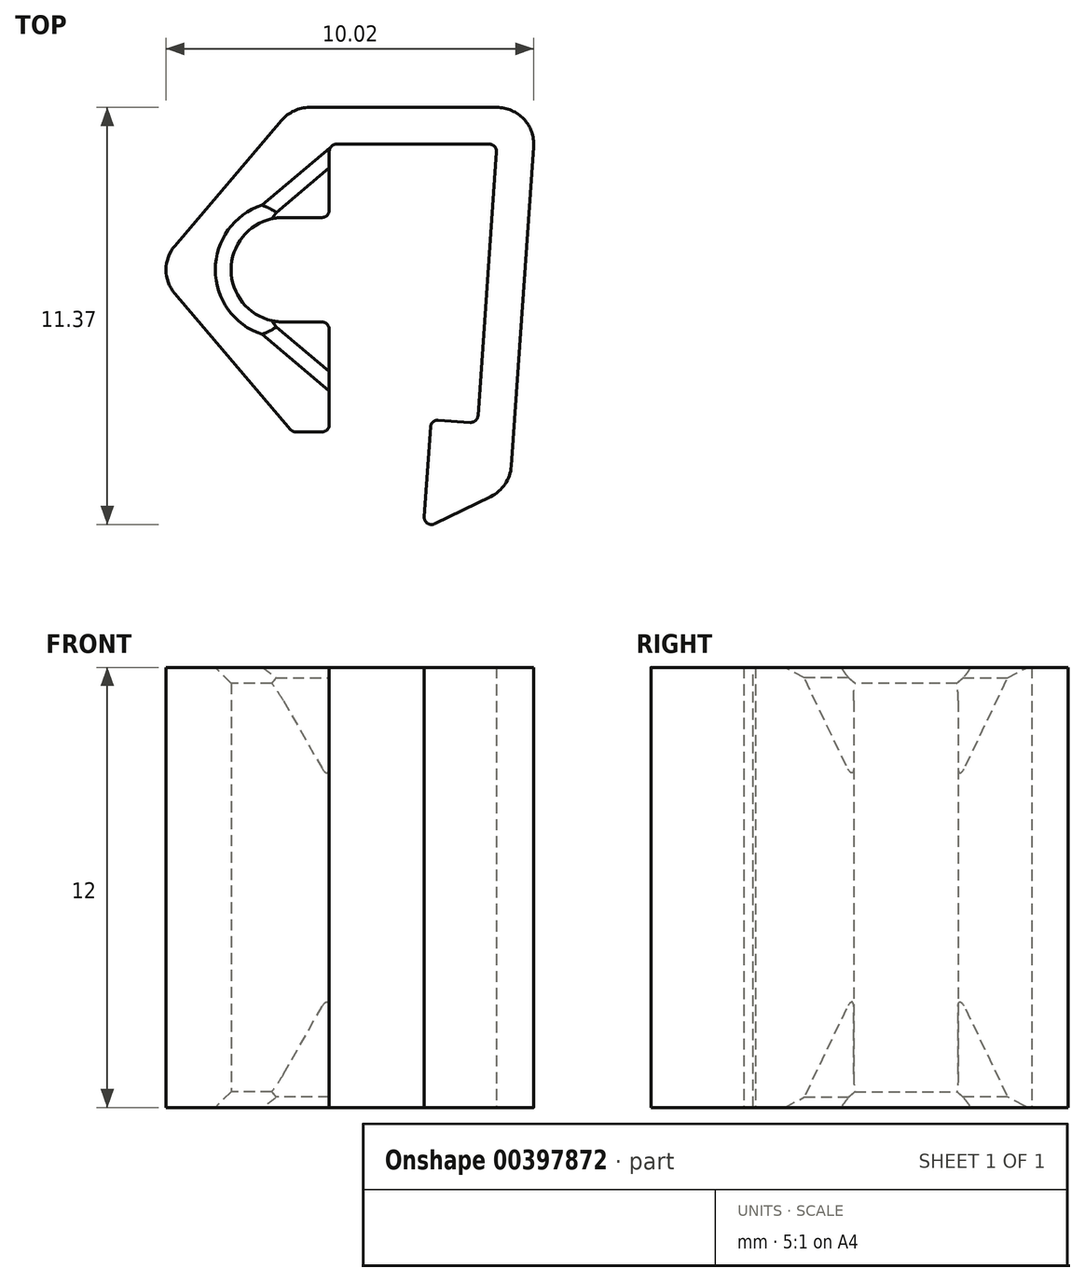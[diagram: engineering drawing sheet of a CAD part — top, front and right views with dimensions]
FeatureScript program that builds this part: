
annotation { "Feature Type Name" : "Feature", "Feature Type Description" : "" }
export const myFeature = defineFeature(function(context is Context, id is Id, definition is map)
    precondition{}
    {
        {
            var Q0;
            Q0=qCreatedBy(makeId("Top.planeOp"),FACE);
            var sketch = newSketch(context, id + "F0", { "sketchPlane" : qUnion([Q0])});
            skLineSegment(sketch, "E0", {"start": v(0, 0) * mm, "end": v(-0.53, -7.6) * mm});
            skLineSegment(sketch, "E1", {"start": v(-0.53, -7.6) * mm, "end": v(-1.8, -7.51) * mm});
            skLineSegment(sketch, "E2", {"start": v(-1.8, -7.51) * mm, "end": v(-2, -10.5) * mm});
            skLineSegment(sketch, "E3", {"start": v(-2, -10.5) * mm, "end": v(0.35, -9.36) * mm});
            skLineSegment(sketch, "E4", {"start": v(0.35, -9.36) * mm, "end": v(1.07, 1) * mm});
            skLineSegment(sketch, "E5", {"start": v(1.07, 1) * mm, "end": v(-5.57, 1) * mm});
            skLineSegment(sketch, "E6", {"start": v(-5.82, -4.85) * mm, "end": v(-4.57, -4.85) * mm});
            skLineSegment(sketch, "E7", {"start": v(-4.57, -4.85) * mm, "end": v(-4.57, -7.85) * mm});
            skLineSegment(sketch, "E8", {"start": v(-9.33, -3.43) * mm, "end": v(-5.57, -7.85) * mm});
            skLineSegment(sketch, "E9", {"start": v(-5.57, -7.85) * mm, "end": v(-4.57, -7.85) * mm});
            skLineSegment(sketch, "E10", {"start": v(-4.57, -2) * mm, "end": v(-5.82, -2) * mm});
            skLineSegment(sketch, "E11", {"start": v(0, 0) * mm, "end": v(-4.57, 0) * mm});
            skLineSegment(sketch, "E12", {"start": v(-4.57, 0) * mm, "end": v(-4.57, -2) * mm});
            skArc(sketch, "E13", {"start": v(-5.82, -2) * mm, "mid": v(-7.25, -3.43) * mm, "end": v(-5.82, -4.85) * mm});
            skLineSegment(sketch, "E14", {"start": v(-9.33, -3.43) * mm, "end": v(-5.57, 1) * mm});
            skLineSegment(sketch, "E15", {"start": v(-5.57, -7.85) * mm, "end": v(-5.57, 1) * mm, "construction": true});
            skLineSegment(sketch, "E16", {"start": v(-5.82, -3.43) * mm, "end": v(-6.9, -2.5) * mm, "construction": true});
            skLineSegment(sketch, "E17", {"start": v(-6.9, -2.5) * mm, "end": v(-7.86, -1.7) * mm, "construction": true});
            skLineSegment(sketch, "E18", {"start": v(0, 0) * mm, "end": v(0, 1) * mm, "construction": true});
            skLineSegment(sketch, "E19", {"start": v(1, -0.07) * mm, "end": v(0, 0) * mm, "construction": true});
            skLineSegment(sketch, "E20", {"start": v(-6.9, -4.35) * mm, "end": v(-7.86, -5.16) * mm, "construction": true});
            skSolve(sketch);
        }
        {
            var Q0;
            Q0=qSketchRegion(id+"F0",true);
            extrude(context, id + "F1", {"entities" : qUnion([Q0]), "depth" : 6 * mm});
        }
        {
            var Q0;
            Q0=makeQuery(id+"F1.opExtrude","CAP_FACE",FACE,{"disambiguationData":[OSD([sQuery(id+"F0.wireOp",EDGE,"E0"),sQuery(id+"F0.wireOp",EDGE,"E1"),sQuery(id+"F0.wireOp",EDGE,"E2"),sQuery(id+"F0.wireOp",EDGE,"E3"),sQuery(id+"F0.wireOp",EDGE,"E4"),sQuery(id+"F0.wireOp",EDGE,"E5"),sQuery(id+"F0.wireOp",EDGE,"3qQk4eZ2-qFBK-7vCE-47k8-9gwiF50xY8QG"),sQuery(id+"F0.wireOp",EDGE,"FwfflrWr-MbD4-lGZ7-AJjG-6BkzjliF19me"),sQuery(id+"F0.wireOp",EDGE,"E6"),sQuery(id+"F0.wireOp",EDGE,"E7"),sQuery(id+"F0.wireOp",EDGE,"dEJFUDGW-VdPt-nXIw-TINV-OlQtnsbTHH9Y"),sQuery(id+"F0.wireOp",EDGE,"E8"),sQuery(id+"F0.wireOp",EDGE,"E9")])],"isStart":false});
            var sketch = newSketch(context, id + "F2", { "sketchPlane" : qUnion([Q0])});
            skLineSegment(sketch, "E21", {"start": v(-6.74, -4.52) * mm, "end": v(-4.57, -6.33) * mm});
            skLineSegment(sketch, "E22", {"start": v(-4.57, -6.33) * mm, "end": v(-4.57, -4.85) * mm});
            skLineSegment(sketch, "E23", {"start": v(-4.57, -4.85) * mm, "end": v(-6.74, -4.52) * mm});
            skLineSegment(sketch, "E24", {"start": v(-6.74, -2.33) * mm, "end": v(-4.57, -0.52) * mm});
            skLineSegment(sketch, "E25", {"start": v(-4.57, -0.52) * mm, "end": v(-4.57, -2) * mm});
            skLineSegment(sketch, "E26", {"start": v(-4.57, -2) * mm, "end": v(-6.74, -2.33) * mm});
            skSolve(sketch);
        }
        {
            var Q0;
            Q0=qSketchRegion(id+"F2",true);
            extrude(context, id + "F3", {"entities" : qUnion([Q0]), "operationType" : NewBodyOperationType.REMOVE, "oppositeDirection" : true, "depth" : 3 * mm});
        }
        {
            var Q0;
            Q0=makeQuery(id+"F3.boolean.opBoolean","COPY",EDGE,{"derivedFrom":makeQuery(id+"F3.opExtrude","CAP_EDGE",EDGE,{"disambiguationData":[OSD([sQuery(id+"F2.wireOp",EDGE,"E21")])],"isStart":false})});
            chamfer(context, id + "F4", {"entities" : qUnion([Q0]), "chamferType" : ChamferType.TWO_OFFSETS, "width1" : 1.1 * mm, "oppositeDirection" : false, "width2" : 3 * mm, "tangentPropagation" : true});
        }
        {
            var Q0;
            Q0=makeQuery(id+"F3.boolean.opBoolean","COPY",EDGE,{"derivedFrom":makeQuery(id+"F3.opExtrude","CAP_EDGE",EDGE,{"disambiguationData":[OSD([sQuery(id+"F2.wireOp",EDGE,"E24")])],"isStart":false})});
            chamfer(context, id + "F5", {"entities" : qUnion([Q0]), "chamferType" : ChamferType.TWO_OFFSETS, "width1" : 3 * mm, "oppositeDirection" : false, "width2" : 1.1 * mm, "tangentPropagation" : true});
        }
        {
            var Q0;
            Q0=makeQuery(id+"F1.opExtrude","SWEPT_EDGE",EDGE,{"disambiguationData":[OSD([sQuery(id+"F0.wireOp",EDGE,"E0"),sQuery(id+"F0.wireOp",EDGE,"3qQk4eZ2-qFBK-7vCE-47k8-9gwiF50xY8QG")])]});
            var Q1;
            Q1=makeQuery(id+"F1.opExtrude","SWEPT_EDGE",EDGE,{"disambiguationData":[OSD([sQuery(id+"F0.wireOp",EDGE,"E0"),sQuery(id+"F0.wireOp",EDGE,"E1")])]});
            var Q2;
            Q2=makeQuery(id+"F1.opExtrude","SWEPT_EDGE",EDGE,{"disambiguationData":[OSD([sQuery(id+"F0.wireOp",EDGE,"E1"),sQuery(id+"F0.wireOp",EDGE,"E2")])]});
            var Q3;
            Q3=makeQuery(id+"F1.opExtrude","SWEPT_EDGE",EDGE,{"disambiguationData":[OSD([sQuery(id+"F0.wireOp",EDGE,"E2"),sQuery(id+"F0.wireOp",EDGE,"E3")])]});
            var Q4;
            Q4=makeQuery(id+"F1.opExtrude","SWEPT_EDGE",EDGE,{"disambiguationData":[OSD([sQuery(id+"F0.wireOp",EDGE,"E7"),sQuery(id+"F0.wireOp",EDGE,"E9")])]});
            var Q5;
            Q5=makeQuery(id+"F1.opExtrude","SWEPT_EDGE",EDGE,{"disambiguationData":[OSD([sQuery(id+"F0.wireOp",EDGE,"E6"),sQuery(id+"F0.wireOp",EDGE,"E7")])]});
            var Q6;
            Q6=makeQuery(id+"F1.opExtrude","SWEPT_EDGE",EDGE,{"disambiguationData":[OSD([sQuery(id+"F0.wireOp",EDGE,"E10"),sQuery(id+"F0.wireOp",EDGE,"E12")])]});
            var Q7;
            Q7=makeQuery(id+"F1.opExtrude","SWEPT_EDGE",EDGE,{"disambiguationData":[OSD([sQuery(id+"F0.wireOp",EDGE,"E8"),sQuery(id+"F0.wireOp",EDGE,"E9")])]});
            var Q8;
            Q8=makeQuery(id+"F1.opExtrude","SWEPT_EDGE",EDGE,{"disambiguationData":[OSD([sQuery(id+"F0.wireOp",EDGE,"E11"),sQuery(id+"F0.wireOp",EDGE,"E12")])]});
            fillet(context, id + "F6", {"entities" : qUnion([Q0, Q1, Q2, Q3, Q4, Q5, Q6, Q7, Q8]), "radius" : .2 * mm, "tangentPropagation" : true, "allowEdgeOverflow" : false});
        }
        {
            var Q0;
            Q0=makeQuery(id+"F1.opExtrude","SWEPT_EDGE",EDGE,{"disambiguationData":[OSD([sQuery(id+"F0.wireOp",EDGE,"E4"),sQuery(id+"F0.wireOp",EDGE,"E5")])]});
            var Q1;
            Q1=makeQuery(id+"F1.opExtrude","SWEPT_EDGE",EDGE,{"disambiguationData":[OSD([sQuery(id+"F0.wireOp",EDGE,"E3"),sQuery(id+"F0.wireOp",EDGE,"E4")])]});
            var Q2;
            Q2=makeQuery(id+"F1.opExtrude","SWEPT_EDGE",EDGE,{"disambiguationData":[OSD([sQuery(id+"F0.wireOp",EDGE,"E8"),sQuery(id+"F0.wireOp",EDGE,"E9")])]});
            var Q3;
            Q3=makeQuery(id+"F1.opExtrude","SWEPT_EDGE",EDGE,{"disambiguationData":[OSD([sQuery(id+"F0.wireOp",EDGE,"E8"),sQuery(id+"F0.wireOp",EDGE,"E14")])]});
            var Q4;
            Q4=makeQuery(id+"F1.opExtrude","SWEPT_EDGE",EDGE,{"disambiguationData":[OSD([sQuery(id+"F0.wireOp",EDGE,"E5"),sQuery(id+"F0.wireOp",EDGE,"E14")])]});
            fillet(context, id + "F7", {"entities" : qUnion([Q0, Q1, Q2, Q3, Q4]), "radius" : 1 * mm, "tangentPropagation" : true, "allowEdgeOverflow" : false});
        }
        {
            var Q0;
            Q0=makeQuery(id+"F1.opExtrude","SWEPT_BODY",BODY,{"disambiguationData":[OSD([sQuery(id+"F0.wireOp",EDGE,"E0"),sQuery(id+"F0.wireOp",EDGE,"E1"),sQuery(id+"F0.wireOp",EDGE,"E2"),sQuery(id+"F0.wireOp",EDGE,"E3"),sQuery(id+"F0.wireOp",EDGE,"E4"),sQuery(id+"F0.wireOp",EDGE,"E5"),sQuery(id+"F0.wireOp",EDGE,"3qQk4eZ2-qFBK-7vCE-47k8-9gwiF50xY8QG"),sQuery(id+"F0.wireOp",EDGE,"FwfflrWr-MbD4-lGZ7-AJjG-6BkzjliF19me"),sQuery(id+"F0.wireOp",EDGE,"E6"),sQuery(id+"F0.wireOp",EDGE,"E7"),sQuery(id+"F0.wireOp",EDGE,"dEJFUDGW-VdPt-nXIw-TINV-OlQtnsbTHH9Y"),sQuery(id+"F0.wireOp",EDGE,"E8"),sQuery(id+"F0.wireOp",EDGE,"E9")])]});
            var Q1;
            Q1=makeQuery(id+"F1.opExtrude","CAP_FACE",FACE,{"disambiguationData":[OSD([sQuery(id+"F0.wireOp",EDGE,"E0"),sQuery(id+"F0.wireOp",EDGE,"E1"),sQuery(id+"F0.wireOp",EDGE,"E2"),sQuery(id+"F0.wireOp",EDGE,"E3"),sQuery(id+"F0.wireOp",EDGE,"E4"),sQuery(id+"F0.wireOp",EDGE,"E5"),sQuery(id+"F0.wireOp",EDGE,"3qQk4eZ2-qFBK-7vCE-47k8-9gwiF50xY8QG"),sQuery(id+"F0.wireOp",EDGE,"FwfflrWr-MbD4-lGZ7-AJjG-6BkzjliF19me"),sQuery(id+"F0.wireOp",EDGE,"E6"),sQuery(id+"F0.wireOp",EDGE,"E7"),sQuery(id+"F0.wireOp",EDGE,"dEJFUDGW-VdPt-nXIw-TINV-OlQtnsbTHH9Y"),sQuery(id+"F0.wireOp",EDGE,"E8"),sQuery(id+"F0.wireOp",EDGE,"E9")])],"isStart":true});
            mirror(context, id + "F8", {"operationType" : NewBodyOperationType.ADD, "entities" : qUnion([Q0]), "mirrorPlane" : qUnion([Q1])});
        }
        {
            var Q0;
            Q0=makeQuery(id+"F1.opExtrude","CAP_EDGE",EDGE,{"disambiguationData":[OSD([sQuery(id+"F0.wireOp",EDGE,"E13")])],"isStart":false});
            var Q1;
            Q1=makeQuery(id+"F8.opPattern","COPY",EDGE,{"derivedFrom":makeQuery(id+"F1.opExtrude","CAP_EDGE",EDGE,{"disambiguationData":[OSD([sQuery(id+"F0.wireOp",EDGE,"E13")])],"isStart":false}),"instanceName":"1"});
            var Q2;
            Q2=makeQuery(id+"F8.opPattern","COPY",EDGE,{"derivedFrom":makeQuery(id+"F5.opChamfer","BLEND_EDGE",EDGE,{"blendedFrom":[makeQuery(id+"F3.boolean.opBoolean","COPY",EDGE,{"derivedFrom":makeQuery(id+"F3.opExtrude","CAP_EDGE",EDGE,{"disambiguationData":[OSD([sQuery(id+"F2.wireOp",EDGE,"E24")])],"isStart":false})}),makeQuery(id+"F1.opExtrude","CAP_FACE",FACE,{"disambiguationData":[OSD([sQuery(id+"F0.wireOp",EDGE,"E0"),sQuery(id+"F0.wireOp",EDGE,"E1"),sQuery(id+"F0.wireOp",EDGE,"E2"),sQuery(id+"F0.wireOp",EDGE,"E3"),sQuery(id+"F0.wireOp",EDGE,"E4"),sQuery(id+"F0.wireOp",EDGE,"E5"),sQuery(id+"F0.wireOp",EDGE,"E6"),sQuery(id+"F0.wireOp",EDGE,"E7"),sQuery(id+"F0.wireOp",EDGE,"E8"),sQuery(id+"F0.wireOp",EDGE,"E9"),sQuery(id+"F0.wireOp",EDGE,"E10"),sQuery(id+"F0.wireOp",EDGE,"E11"),sQuery(id+"F0.wireOp",EDGE,"E12"),sQuery(id+"F0.wireOp",EDGE,"E13"),sQuery(id+"F0.wireOp",EDGE,"E14")])],"isStart":false})],"blendedInto":[makeQuery(id+"F1.opExtrude","CAP_FACE",FACE,{"disambiguationData":[OSD([sQuery(id+"F0.wireOp",EDGE,"E0"),sQuery(id+"F0.wireOp",EDGE,"E1"),sQuery(id+"F0.wireOp",EDGE,"E2"),sQuery(id+"F0.wireOp",EDGE,"E3"),sQuery(id+"F0.wireOp",EDGE,"E4"),sQuery(id+"F0.wireOp",EDGE,"E5"),sQuery(id+"F0.wireOp",EDGE,"E6"),sQuery(id+"F0.wireOp",EDGE,"E7"),sQuery(id+"F0.wireOp",EDGE,"E8"),sQuery(id+"F0.wireOp",EDGE,"E9"),sQuery(id+"F0.wireOp",EDGE,"E10"),sQuery(id+"F0.wireOp",EDGE,"E11"),sQuery(id+"F0.wireOp",EDGE,"E12"),sQuery(id+"F0.wireOp",EDGE,"E13"),sQuery(id+"F0.wireOp",EDGE,"E14")])],"isStart":false})]}),"instanceName":"1"});
            var Q3;
            Q3=makeQuery(id+"F8.opPattern","COPY",EDGE,{"derivedFrom":makeQuery(id+"F4.opChamfer","BLEND_EDGE",EDGE,{"blendedFrom":[makeQuery(id+"F3.boolean.opBoolean","COPY",EDGE,{"derivedFrom":makeQuery(id+"F3.opExtrude","CAP_EDGE",EDGE,{"disambiguationData":[OSD([sQuery(id+"F2.wireOp",EDGE,"E21")])],"isStart":false})}),makeQuery(id+"F1.opExtrude","CAP_FACE",FACE,{"disambiguationData":[OSD([sQuery(id+"F0.wireOp",EDGE,"E0"),sQuery(id+"F0.wireOp",EDGE,"E1"),sQuery(id+"F0.wireOp",EDGE,"E2"),sQuery(id+"F0.wireOp",EDGE,"E3"),sQuery(id+"F0.wireOp",EDGE,"E4"),sQuery(id+"F0.wireOp",EDGE,"E5"),sQuery(id+"F0.wireOp",EDGE,"E6"),sQuery(id+"F0.wireOp",EDGE,"E7"),sQuery(id+"F0.wireOp",EDGE,"E8"),sQuery(id+"F0.wireOp",EDGE,"E9"),sQuery(id+"F0.wireOp",EDGE,"E10"),sQuery(id+"F0.wireOp",EDGE,"E11"),sQuery(id+"F0.wireOp",EDGE,"E12"),sQuery(id+"F0.wireOp",EDGE,"E13"),sQuery(id+"F0.wireOp",EDGE,"E14")])],"isStart":false})],"blendedInto":[makeQuery(id+"F1.opExtrude","CAP_FACE",FACE,{"disambiguationData":[OSD([sQuery(id+"F0.wireOp",EDGE,"E0"),sQuery(id+"F0.wireOp",EDGE,"E1"),sQuery(id+"F0.wireOp",EDGE,"E2"),sQuery(id+"F0.wireOp",EDGE,"E3"),sQuery(id+"F0.wireOp",EDGE,"E4"),sQuery(id+"F0.wireOp",EDGE,"E5"),sQuery(id+"F0.wireOp",EDGE,"E6"),sQuery(id+"F0.wireOp",EDGE,"E7"),sQuery(id+"F0.wireOp",EDGE,"E8"),sQuery(id+"F0.wireOp",EDGE,"E9"),sQuery(id+"F0.wireOp",EDGE,"E10"),sQuery(id+"F0.wireOp",EDGE,"E11"),sQuery(id+"F0.wireOp",EDGE,"E12"),sQuery(id+"F0.wireOp",EDGE,"E13"),sQuery(id+"F0.wireOp",EDGE,"E14")])],"isStart":false})]}),"instanceName":"1"});
            var Q4;
            Q4=makeQuery(id+"F4.opChamfer","BLEND_EDGE",EDGE,{"blendedFrom":[makeQuery(id+"F3.boolean.opBoolean","COPY",EDGE,{"derivedFrom":makeQuery(id+"F3.opExtrude","CAP_EDGE",EDGE,{"disambiguationData":[OSD([sQuery(id+"F2.wireOp",EDGE,"E21")])],"isStart":false})}),makeQuery(id+"F1.opExtrude","CAP_FACE",FACE,{"disambiguationData":[OSD([sQuery(id+"F0.wireOp",EDGE,"E0"),sQuery(id+"F0.wireOp",EDGE,"E1"),sQuery(id+"F0.wireOp",EDGE,"E2"),sQuery(id+"F0.wireOp",EDGE,"E3"),sQuery(id+"F0.wireOp",EDGE,"E4"),sQuery(id+"F0.wireOp",EDGE,"E5"),sQuery(id+"F0.wireOp",EDGE,"E6"),sQuery(id+"F0.wireOp",EDGE,"E7"),sQuery(id+"F0.wireOp",EDGE,"E8"),sQuery(id+"F0.wireOp",EDGE,"E9"),sQuery(id+"F0.wireOp",EDGE,"E10"),sQuery(id+"F0.wireOp",EDGE,"E11"),sQuery(id+"F0.wireOp",EDGE,"E12"),sQuery(id+"F0.wireOp",EDGE,"E13"),sQuery(id+"F0.wireOp",EDGE,"E14")])],"isStart":false})],"blendedInto":[makeQuery(id+"F1.opExtrude","CAP_FACE",FACE,{"disambiguationData":[OSD([sQuery(id+"F0.wireOp",EDGE,"E0"),sQuery(id+"F0.wireOp",EDGE,"E1"),sQuery(id+"F0.wireOp",EDGE,"E2"),sQuery(id+"F0.wireOp",EDGE,"E3"),sQuery(id+"F0.wireOp",EDGE,"E4"),sQuery(id+"F0.wireOp",EDGE,"E5"),sQuery(id+"F0.wireOp",EDGE,"E6"),sQuery(id+"F0.wireOp",EDGE,"E7"),sQuery(id+"F0.wireOp",EDGE,"E8"),sQuery(id+"F0.wireOp",EDGE,"E9"),sQuery(id+"F0.wireOp",EDGE,"E10"),sQuery(id+"F0.wireOp",EDGE,"E11"),sQuery(id+"F0.wireOp",EDGE,"E12"),sQuery(id+"F0.wireOp",EDGE,"E13"),sQuery(id+"F0.wireOp",EDGE,"E14")])],"isStart":false})]});
            var Q5;
            Q5=makeQuery(id+"F5.opChamfer","BLEND_EDGE",EDGE,{"blendedFrom":[makeQuery(id+"F3.boolean.opBoolean","COPY",EDGE,{"derivedFrom":makeQuery(id+"F3.opExtrude","CAP_EDGE",EDGE,{"disambiguationData":[OSD([sQuery(id+"F2.wireOp",EDGE,"E24")])],"isStart":false})}),makeQuery(id+"F1.opExtrude","CAP_FACE",FACE,{"disambiguationData":[OSD([sQuery(id+"F0.wireOp",EDGE,"E0"),sQuery(id+"F0.wireOp",EDGE,"E1"),sQuery(id+"F0.wireOp",EDGE,"E2"),sQuery(id+"F0.wireOp",EDGE,"E3"),sQuery(id+"F0.wireOp",EDGE,"E4"),sQuery(id+"F0.wireOp",EDGE,"E5"),sQuery(id+"F0.wireOp",EDGE,"E6"),sQuery(id+"F0.wireOp",EDGE,"E7"),sQuery(id+"F0.wireOp",EDGE,"E8"),sQuery(id+"F0.wireOp",EDGE,"E9"),sQuery(id+"F0.wireOp",EDGE,"E10"),sQuery(id+"F0.wireOp",EDGE,"E11"),sQuery(id+"F0.wireOp",EDGE,"E12"),sQuery(id+"F0.wireOp",EDGE,"E13"),sQuery(id+"F0.wireOp",EDGE,"E14")])],"isStart":false})],"blendedInto":[makeQuery(id+"F1.opExtrude","CAP_FACE",FACE,{"disambiguationData":[OSD([sQuery(id+"F0.wireOp",EDGE,"E0"),sQuery(id+"F0.wireOp",EDGE,"E1"),sQuery(id+"F0.wireOp",EDGE,"E2"),sQuery(id+"F0.wireOp",EDGE,"E3"),sQuery(id+"F0.wireOp",EDGE,"E4"),sQuery(id+"F0.wireOp",EDGE,"E5"),sQuery(id+"F0.wireOp",EDGE,"E6"),sQuery(id+"F0.wireOp",EDGE,"E7"),sQuery(id+"F0.wireOp",EDGE,"E8"),sQuery(id+"F0.wireOp",EDGE,"E9"),sQuery(id+"F0.wireOp",EDGE,"E10"),sQuery(id+"F0.wireOp",EDGE,"E11"),sQuery(id+"F0.wireOp",EDGE,"E12"),sQuery(id+"F0.wireOp",EDGE,"E13"),sQuery(id+"F0.wireOp",EDGE,"E14")])],"isStart":false})]});
            chamfer(context, id + "F9", {"entities" : qUnion([Q0, Q1, Q2, Q3, Q4, Q5]), "chamferType" : ChamferType.OFFSET_ANGLE, "width" : .43 * mm, "oppositeDirection" : false, "angle" : 45 * degree, "tangentPropagation" : true});
        }
    });
